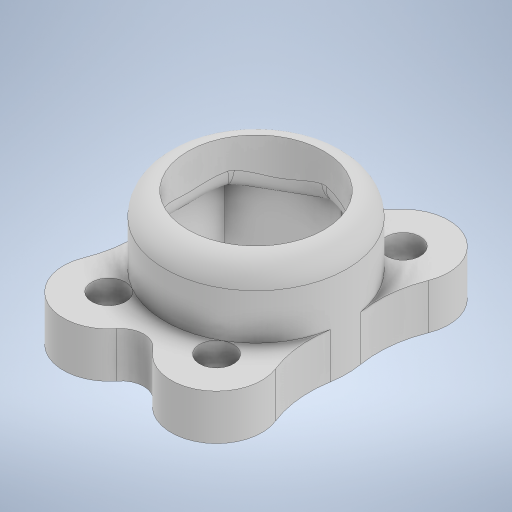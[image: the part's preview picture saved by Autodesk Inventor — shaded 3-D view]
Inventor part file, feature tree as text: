
AUTODESK INVENTOR PART (.ipt)
format: ipt  version: 2023 (Build 270158000, 158)  size: 455,168 bytes
history: native  units: mm
features: sketch x5, extrude x4, fillet x4, hole x1, projected_geometry x1
ambient origin geometry x8: Origin, YZ Plane, XZ Plane, XY Plane, X Axis, Y Axis, Z Axis, Center Point
bodies: Solid1 (feature_tree)
feature tree (15):
  extrude  "Extrusion1"  Depth=9.5mm
  extrude  "Extrusion2"  Depth=9.5mm
  extrude  "Extrusion3"  Depth=8.0mm
  extrude  "Extrusion4"  Depth=4.0mm TaperAngle=0.0deg
  fillet  "Fillet1"  Radius=6.0mm
  hole  "Hole1"  [1 undecoded]
  fillet  "Fillet2"  Radius=13.0mm
  fillet  "Fillet4"  Radius=5.5mm
  fillet  "Fillet5"  Radius=2.0mm
  sketch  "Sketch1"  dims[d0=8.0mm d1=8.0mm d2=9.5mm]
  sketch  "Sketch2"  dims[d3=8.0mm d5=9.5mm]
  sketch  "Sketch3"  dims[d9=8.0mm d10=8.0mm]
  sketch  "Sketch4"  dims[d11=16.0mm d13=4.0mm d14=0.0mm d15=6.0mm d16=0.0mm]
  sketch  "Sketch5"  dims[d17=12.0mm d18=6.0mm d19=0.0mm d20=13.0mm d21=5.5mm d22=0.0mm d23=2.0mm d24=3.0mm d25=6.0mm d26=5.5mm d27=2.0mm d28=90.0deg d29=8.0mm d30=20.594885mm d31=2.0mm d33=2.0mm d34=10.0mm]
  projected_geometry  "Projected Loop1"
note: 1 required parameter value undecoded (feature->parameter linkage not recoverable at this tier; creation-order binding heuristic only, values carry confidence <= 0.55)
